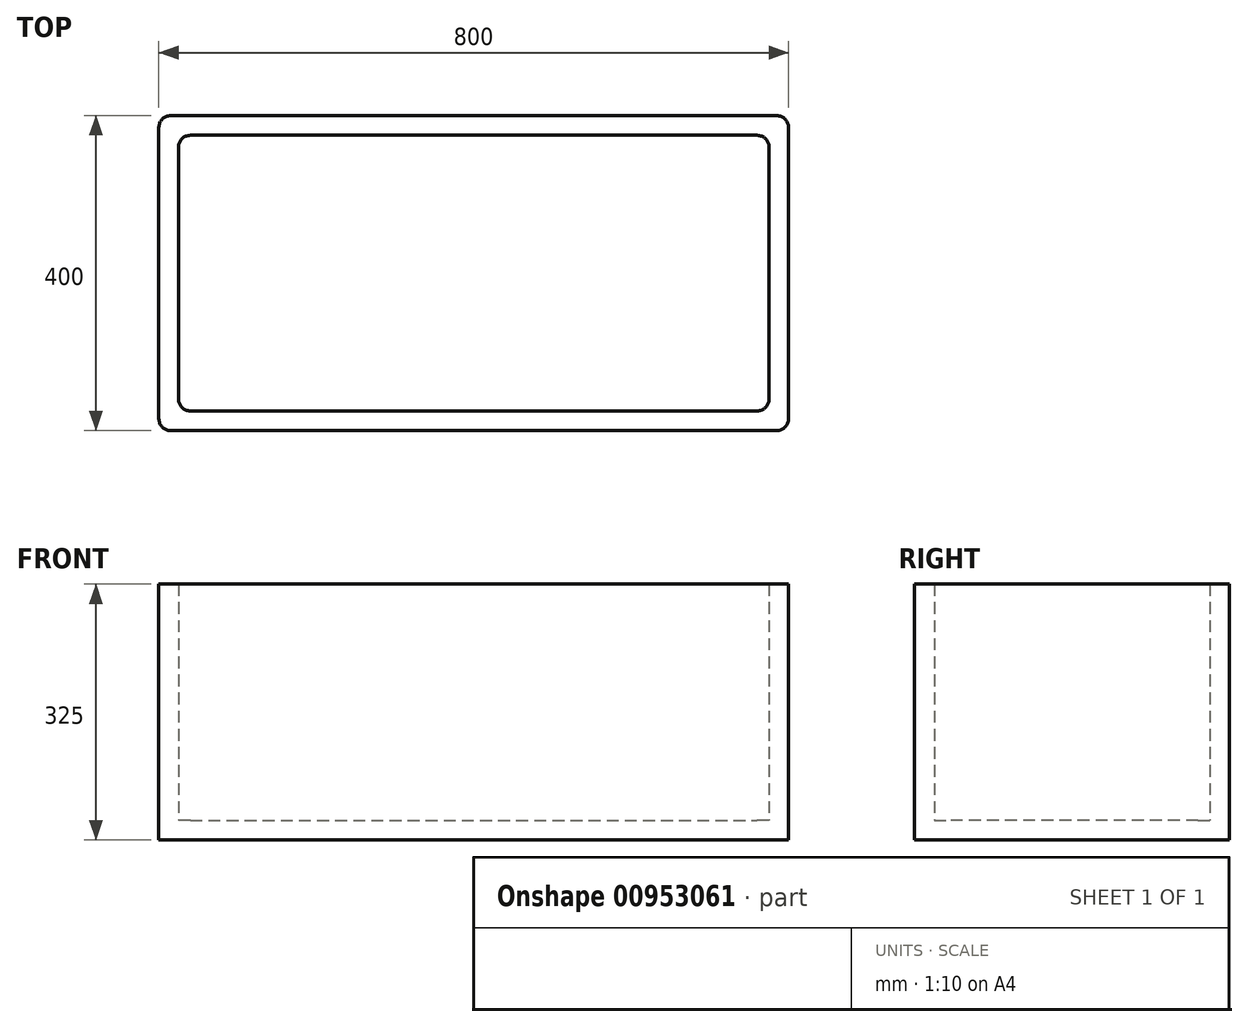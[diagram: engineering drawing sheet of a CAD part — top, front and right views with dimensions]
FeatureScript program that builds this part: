
annotation { "Feature Type Name" : "Feature", "Feature Type Description" : "" }
export const myFeature = defineFeature(function(context is Context, id is Id, definition is map)
    precondition{}
    {
        {
            var Q0;
            Q0=qCreatedBy(makeId("Top.planeOp"),FACE);
            var sketch = newSketch(context, id + "F0", { "sketchPlane" : qUnion([Q0])});
            skLineSegment(sketch, "E0.bottom", {"start": v(0, 0) * mm, "end": v(800, 0) * mm});
            skLineSegment(sketch, "E0.top", {"start": v(0, 400) * mm, "end": v(800, 400) * mm});
            skLineSegment(sketch, "E0.left", {"start": v(0, 0) * mm, "end": v(0, 400) * mm});
            skLineSegment(sketch, "E0.right", {"start": v(800, 0) * mm, "end": v(800, 400) * mm});
            skLineSegment(sketch, "E1.bottom", {"start": v(25, 375) * mm, "end": v(775, 375) * mm});
            skLineSegment(sketch, "E1.top", {"start": v(25, 25) * mm, "end": v(775, 25) * mm});
            skLineSegment(sketch, "E1.left", {"start": v(25, 375) * mm, "end": v(25, 25) * mm});
            skLineSegment(sketch, "E1.right", {"start": v(775, 375) * mm, "end": v(775, 25) * mm});
            skSolve(sketch);
        }
        {
            var Q0;
            Q0=makeQuery(id+"F0.imprint","IMPRINT",FACE,{"disambiguationData":[TD([[makeQuery(id+"F0.imprint","IMPRINT",EDGE,{"derivedFrom":sQuery(id+"F0.wireOp",EDGE,"E0.bottom")}),1.0]])]});
            extrude(context, id + "F1", {"entities" : qUnion([Q0]), "depth" : 300 * mm, "offsetDistance" : 25 * mm});
        }
        {
            var Q0;
            Q0=makeQuery(id+"F1.opExtrude","SWEPT_EDGE",EDGE,{"disambiguationData":[OSD([sQuery(id+"F0.wireOp",EDGE,"E0.bottom"),sQuery(id+"F0.wireOp",EDGE,"E0.left")])]});
            var Q1;
            Q1=makeQuery(id+"F1.opExtrude","SWEPT_EDGE",EDGE,{"disambiguationData":[OSD([sQuery(id+"F0.wireOp",EDGE,"E0.bottom"),sQuery(id+"F0.wireOp",EDGE,"E0.right")])]});
            var Q2;
            Q2=makeQuery(id+"F1.opExtrude","SWEPT_EDGE",EDGE,{"disambiguationData":[OSD([sQuery(id+"F0.wireOp",EDGE,"E0.top"),sQuery(id+"F0.wireOp",EDGE,"E0.left")])]});
            var Q3;
            Q3=makeQuery(id+"F1.opExtrude","SWEPT_EDGE",EDGE,{"disambiguationData":[OSD([sQuery(id+"F0.wireOp",EDGE,"E0.top"),sQuery(id+"F0.wireOp",EDGE,"E0.right")])]});
            var Q4;
            Q4=makeQuery(id+"F1.opExtrude","SWEPT_EDGE",EDGE,{"disambiguationData":[OSD([sQuery(id+"F0.wireOp",EDGE,"E1.top"),sQuery(id+"F0.wireOp",EDGE,"E1.left")])]});
            var Q5;
            Q5=makeQuery(id+"F1.opExtrude","SWEPT_EDGE",EDGE,{"disambiguationData":[OSD([sQuery(id+"F0.wireOp",EDGE,"E1.bottom"),sQuery(id+"F0.wireOp",EDGE,"E1.left")])]});
            var Q6;
            Q6=makeQuery(id+"F1.opExtrude","SWEPT_EDGE",EDGE,{"disambiguationData":[OSD([sQuery(id+"F0.wireOp",EDGE,"E1.top"),sQuery(id+"F0.wireOp",EDGE,"E1.right")])]});
            var Q7;
            Q7=makeQuery(id+"F1.opExtrude","SWEPT_EDGE",EDGE,{"disambiguationData":[OSD([sQuery(id+"F0.wireOp",EDGE,"E1.bottom"),sQuery(id+"F0.wireOp",EDGE,"E1.right")])]});
            fillet(context, id + "F2", {"entities" : qUnion([Q0, Q1, Q2, Q3, Q4, Q5, Q6, Q7]), "radius" : 15 * mm, "tangentPropagation" : true, "allowEdgeOverflow" : false});
        }
        {
            var Q0;
            Q0=makeQuery(id+"F1.opExtrude","CAP_FACE",FACE,{"disambiguationData":[OSD([sQuery(id+"F0.wireOp",EDGE,"E0.bottom"),sQuery(id+"F0.wireOp",EDGE,"E0.top"),sQuery(id+"F0.wireOp",EDGE,"E0.left"),sQuery(id+"F0.wireOp",EDGE,"E0.right"),sQuery(id+"F0.wireOp",EDGE,"E1.bottom"),sQuery(id+"F0.wireOp",EDGE,"E1.top"),sQuery(id+"F0.wireOp",EDGE,"E1.left"),sQuery(id+"F0.wireOp",EDGE,"E1.right")])],"isStart":true});
            var sketch = newSketch(context, id + "F3", { "sketchPlane" : qUnion([Q0])});
            skLineSegment(sketch, "E2.bottom", {"start": v(785, 0) * mm, "end": v(15, 0) * mm});
            skLineSegment(sketch, "E2.top", {"start": v(785, -400) * mm, "end": v(15, -400) * mm});
            skLineSegment(sketch, "E2.left", {"start": v(800, -15) * mm, "end": v(800, -385) * mm});
            skLineSegment(sketch, "E2.right", {"start": v(0, -15) * mm, "end": v(0, -385) * mm});
            skPoint(sketch, "E3.visualSharp", {"position": v(0, -400) * mm});
            skArc(sketch, "E3.filletArc", {"start": v(0, -385) * mm, "mid": v(4.4, -395.6) * mm, "end": v(15, -400) * mm});
            skPoint(sketch, "E4.visualSharp", {"position": v(0, 0) * mm});
            skArc(sketch, "E4.filletArc", {"start": v(15, 0) * mm, "mid": v(4.4, -4.4) * mm, "end": v(0, -15) * mm});
            skPoint(sketch, "E5.visualSharp", {"position": v(800, 0) * mm});
            skArc(sketch, "E5.filletArc", {"start": v(800, -15) * mm, "mid": v(795.6, -4.4) * mm, "end": v(785, 0) * mm});
            skPoint(sketch, "E6.visualSharp", {"position": v(800, -400) * mm});
            skArc(sketch, "E6.filletArc", {"start": v(785, -400) * mm, "mid": v(795.6, -395.6) * mm, "end": v(800, -385) * mm});
            skSolve(sketch);
        }
        {
            var Q0;
            Q0 = qSketchRegion(id + "F3", true);
            extrude(context, id + "F4", {"entities" : qUnion([Q0]), "operationType" : NewBodyOperationType.ADD, "depth" : 25 * mm, "offsetDistance" : 25 * mm});
        }
    });
